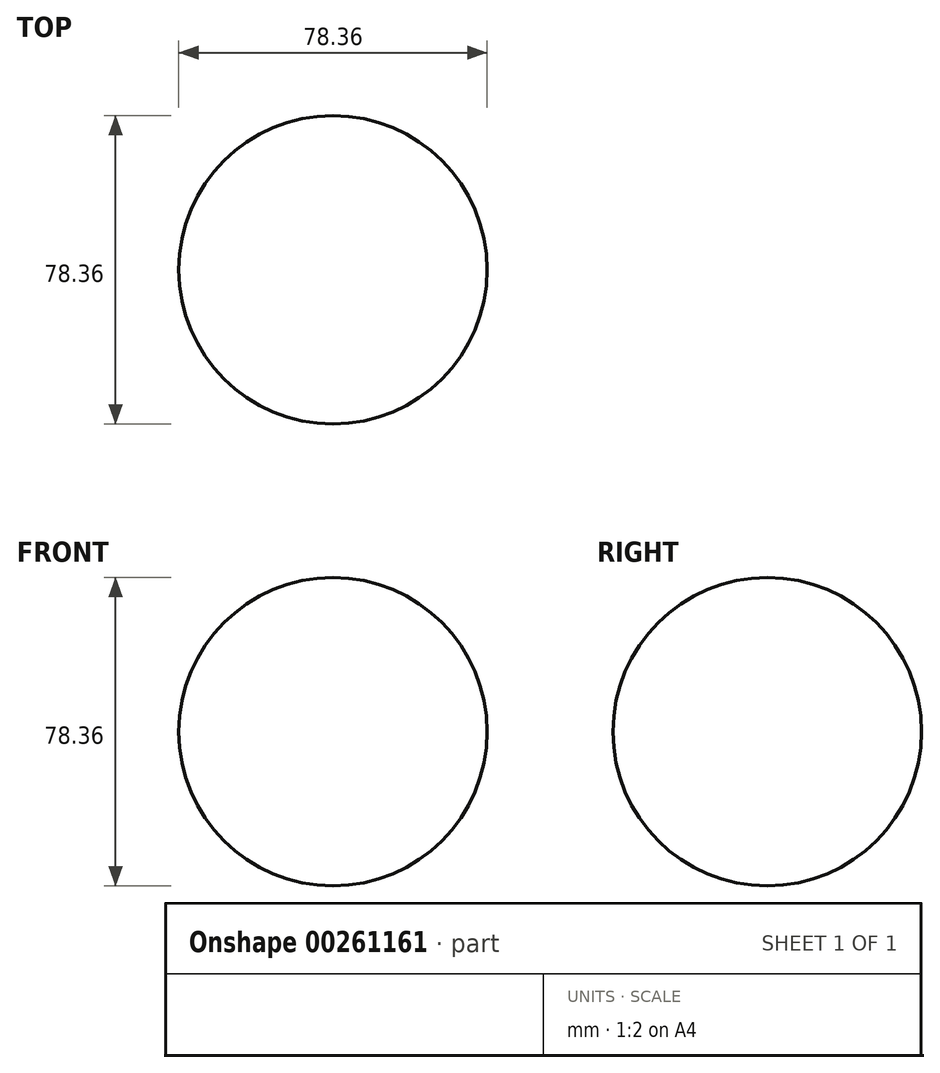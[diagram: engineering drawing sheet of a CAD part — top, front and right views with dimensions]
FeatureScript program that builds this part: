
annotation { "Feature Type Name" : "Feature", "Feature Type Description" : "" }
export const myFeature = defineFeature(function(context is Context, id is Id, definition is map)
    precondition{}
    {
        {
            var Q0;
            Q0=qCreatedBy(makeId("Front.planeOp"),FACE);
            var sketch = newSketch(context, id + "F0", { "sketchPlane" : qUnion([Q0])});
            skArc(sketch, "E0", {"start": v(0, 39.18) * mm, "mid": v(39.18, 0) * mm, "end": v(0, -39.18) * mm});
            skLineSegment(sketch, "E1", {"start": v(0, 39.18) * mm, "end": v(0, -39.18) * mm});
            skLineSegment(sketch, "E2", {"start": v(0, 55.64) * mm, "end": v(0, -55.38) * mm, "construction": true});
            skSolve(sketch);
        }
        {
            var Q0;
            Q0 = qSketchRegion(id + "F0", true);
            var Q1;
            Q1=sQuery(id+"F0.wireOp",EDGE,"E2");
            revolve(context, id + "F1", {"entities" : qUnion([Q0]), "axis" : qUnion([Q1]), "revolveType" : RevolveType.FULL});
        }
    });
